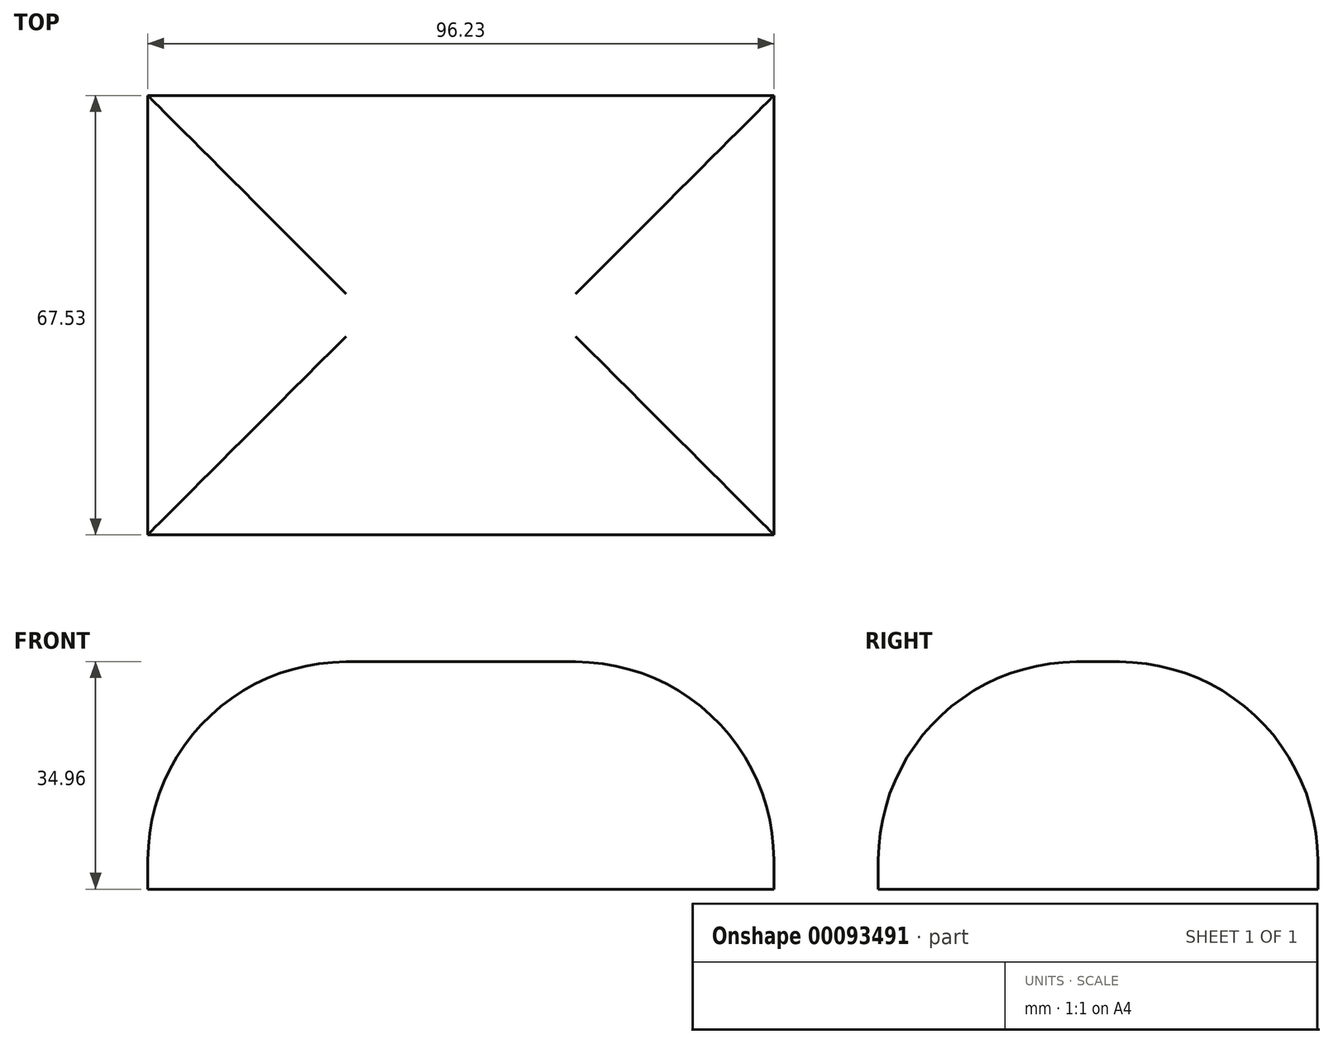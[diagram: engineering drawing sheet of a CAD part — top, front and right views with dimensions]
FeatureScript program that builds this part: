
annotation { "Feature Type Name" : "Feature", "Feature Type Description" : "" }
export const myFeature = defineFeature(function(context is Context, id is Id, definition is map)
    precondition{}
    {
        {
            var Q0;
            Q0=qCreatedBy(makeId("Top.planeOp"),FACE);
            var sketch = newSketch(context, id + "F0", { "sketchPlane" : qUnion([Q0])});
            skLineSegment(sketch, "E0.bottom", {"start": v(0, 0) * mm, "end": v(-96.23, 0) * mm});
            skLineSegment(sketch, "E0.top", {"start": v(0, -67.53) * mm, "end": v(-96.23, -67.53) * mm});
            skLineSegment(sketch, "E0.left", {"start": v(0, 0) * mm, "end": v(0, -67.53) * mm});
            skLineSegment(sketch, "E0.right", {"start": v(-96.23, 0) * mm, "end": v(-96.23, -67.53) * mm});
            skSolve(sketch);
        }
        {
            var Q0;
            Q0 = qSketchRegion(id + "FdwVXmLWgskLqnt_0", true);
            var Q1;
            Q1=makeQuery(id+"F0.imprint","IMPRINT",FACE,{"disambiguationData":[TD([[makeQuery(id+"F0.imprint","IMPRINT",EDGE,{"derivedFrom":sQuery(id+"F0.wireOp",EDGE,"E0.bottom")}),1.0]])]});
            extrude(context, id + "F1", {"entities" : qUnion([Q0, Q1]), "depth" : 34.96 * mm});
        }
        {
            var Q0;
            Q0=makeQuery(id+"F1.opExtrude","CAP_FACE",FACE,{"disambiguationData":[OSD([sQuery(id+"F0.wireOp",EDGE,"E0.bottom"),sQuery(id+"F0.wireOp",EDGE,"E0.top"),sQuery(id+"F0.wireOp",EDGE,"E0.left"),sQuery(id+"F0.wireOp",EDGE,"E0.right")])],"isStart":false});
            fillet(context, id + "F2", {"entities" : qUnion([Q0]), "radius" : 30.48 * mm, "tangentPropagation" : true, "allowEdgeOverflow" : false});
        }
    });
